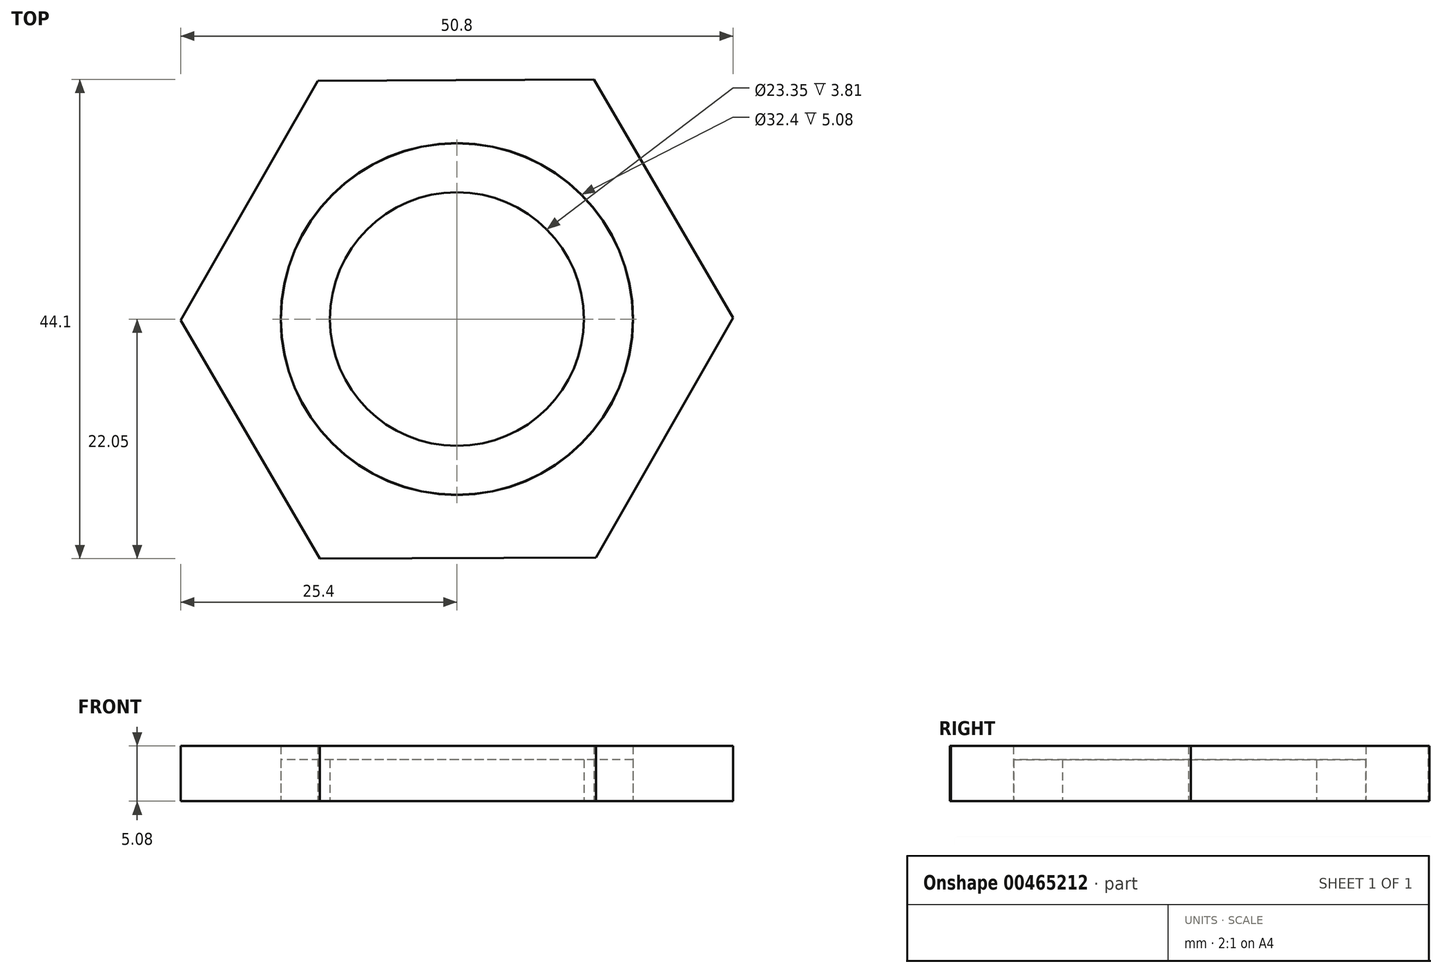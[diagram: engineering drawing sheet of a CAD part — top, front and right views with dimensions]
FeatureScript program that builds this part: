
annotation { "Feature Type Name" : "Feature", "Feature Type Description" : "" }
export const myFeature = defineFeature(function(context is Context, id is Id, definition is map)
    precondition{}
    {
        {
            var Q0;
            Q0=qCreatedBy(makeId("Top.planeOp"),FACE);
            var sketch = newSketch(context, id + "F0", { "sketchPlane" : qUnion([Q0])});
            skCircle(sketch, "E0", {"center": v(0, 0) * mm, "radius": 16.2 * mm});
            skCircle(sketch, "E1", {"center": v(0, 0) * mm, "radius": 11.68 * mm});
            skCircle(sketch, "E2", {"center": v(0, 0) * mm, "radius": 16.18 * mm});
            skCircle(sketch, "E3.cCircle", {"center": v(0, 0) * mm, "radius": 25.4 * mm, "construction": true});
            skLineSegment(sketch, "E3.0", {"start": v(-12.8, 21.94) * mm, "end": v(12.6, 22.05) * mm});
            skLineSegment(sketch, "E3.1", {"start": v(12.6, 22.05) * mm, "end": v(25.4, 0.11) * mm});
            skLineSegment(sketch, "E3.2", {"start": v(25.4, 0.11) * mm, "end": v(12.8, -21.94) * mm});
            skLineSegment(sketch, "E3.3", {"start": v(12.8, -21.94) * mm, "end": v(-12.6, -22.05) * mm});
            skLineSegment(sketch, "E3.4", {"start": v(-12.6, -22.05) * mm, "end": v(-25.4, -0.11) * mm});
            skLineSegment(sketch, "E3.5", {"start": v(-25.4, -0.11) * mm, "end": v(-12.8, 21.94) * mm});
            skSolve(sketch);
        }
        {
            var Q0;
            Q0=qSketchRegion(id+"F0",true);
            extrude(context, id + "F1", {"entities" : qUnion([Q0]), "depth" : 5.08 * mm});
        }
        {
            var Q0;
            Q0=makeQuery(id+"F0.imprint","IMPRINT",FACE,{"disambiguationData":[TD([[makeQuery(id+"F0.imprint","IMPRINT",EDGE,{"derivedFrom":sQuery(id+"F0.wireOp",EDGE,"E1")}),-1.0]])]});
            extrude(context, id + "F2", {"entities" : qUnion([Q0]), "depth" : 3.8 * mm});
        }
    });
